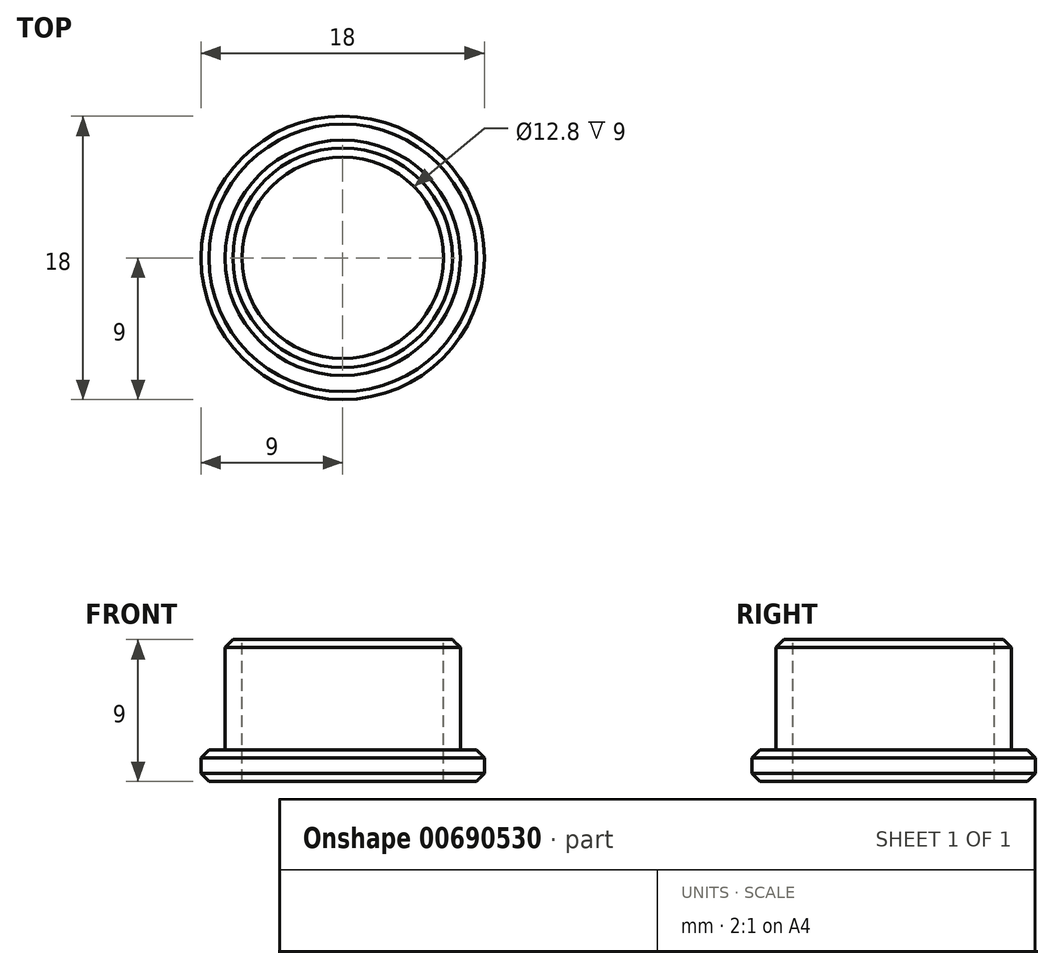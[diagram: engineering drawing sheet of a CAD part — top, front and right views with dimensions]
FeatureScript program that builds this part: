
annotation { "Feature Type Name" : "Feature", "Feature Type Description" : "" }
export const myFeature = defineFeature(function(context is Context, id is Id, definition is map)
    precondition{}
    {
        {
            var Q0;
            Q0=qCreatedBy(makeId("Top.planeOp"),FACE);
            var sketch = newSketch(context, id + "F0", { "sketchPlane" : qUnion([Q0])});
            skCircle(sketch, "E0", {"center": v(0, 0) * mm, "radius": 9 * mm});
            skSolve(sketch);
        }
        {
            var Q0;
            Q0 = qSketchRegion(id + "F0", true);
            extrude(context, id + "F1", {"entities" : qUnion([Q0]), "depth" : 2 * mm, "offsetDistance" : 25 * mm});
        }
        {
            var Q0;
            Q0=makeQuery(id+"F1.opExtrude","CAP_FACE",FACE,{"disambiguationData":[OSD([sQuery(id+"F0.wireOp",EDGE,"E0")])],"isStart":false});
            var sketch = newSketch(context, id + "F2", { "sketchPlane" : qUnion([Q0])});
            skCircle(sketch, "E1", {"center": v(0, 0) * mm, "radius": 7.48 * mm});
            skSolve(sketch);
        }
        {
            var Q0;
            Q0=makeQuery(id+"F2.imprint","IMPRINT",FACE,{"disambiguationData":[TD([[makeQuery(id+"F2.imprint","IMPRINT",EDGE,{"derivedFrom":sQuery(id+"F2.wireOp",EDGE,"E1")}),1.0]])]});
            extrude(context, id + "F3", {"entities" : qUnion([Q0]), "operationType" : NewBodyOperationType.ADD, "depth" : 7 * mm, "offsetDistance" : 25 * mm});
        }
        {
            var Q0;
            Q0=makeQuery(id+"F3.opExtrude","CAP_FACE",FACE,{"disambiguationData":[OSD([sQuery(id+"F2.wireOp",EDGE,"E1")])],"isStart":false});
            var sketch = newSketch(context, id + "F4", { "sketchPlane" : qUnion([Q0])});
            skCircle(sketch, "E2", {"center": v(0, 0) * mm, "radius": 6.4 * mm});
            skSolve(sketch);
        }
        {
            var Q0;
            Q0=makeQuery(id+"F4.imprint","IMPRINT",FACE,{"disambiguationData":[TD([[makeQuery(id+"F4.imprint","IMPRINT",EDGE,{"derivedFrom":sQuery(id+"F4.wireOp",EDGE,"E2")}),1.0]])]});
            extrude(context, id + "F5", {"entities" : qUnion([Q0]), "operationType" : NewBodyOperationType.REMOVE, "oppositeDirection" : true, "depth" : 25 * mm, "offsetDistance" : 25 * mm});
        }
        {
            var Q0;
            Q0=makeQuery(id+"F3.opExtrude","CAP_EDGE",EDGE,{"disambiguationData":[OSD([sQuery(id+"F2.wireOp",EDGE,"E1")])],"isStart":false});
            var Q1;
            Q1=makeQuery(id+"F1.opExtrude","CAP_EDGE",EDGE,{"disambiguationData":[OSD([sQuery(id+"F0.wireOp",EDGE,"E0")])],"isStart":false});
            var Q2;
            Q2=makeQuery(id+"F1.opExtrude","CAP_EDGE",EDGE,{"disambiguationData":[OSD([sQuery(id+"F0.wireOp",EDGE,"E0")])],"isStart":true});
            var Q3;
            Q3=makeQuery(id+"F5.boolean.opBoolean","COPY",EDGE,{"derivedFrom":makeQuery(id+"F5.opExtrude","CAP_EDGE",EDGE,{"disambiguationData":[OSD([sQuery(id+"F4.wireOp",EDGE,"E2")])],"isStart":true})});
            chamfer(context, id + "F6", {"entities" : qUnion([Q0, Q1, Q2, Q3]), "width" : 0.5 * mm, "tangentPropagation" : true});
        }
    });
